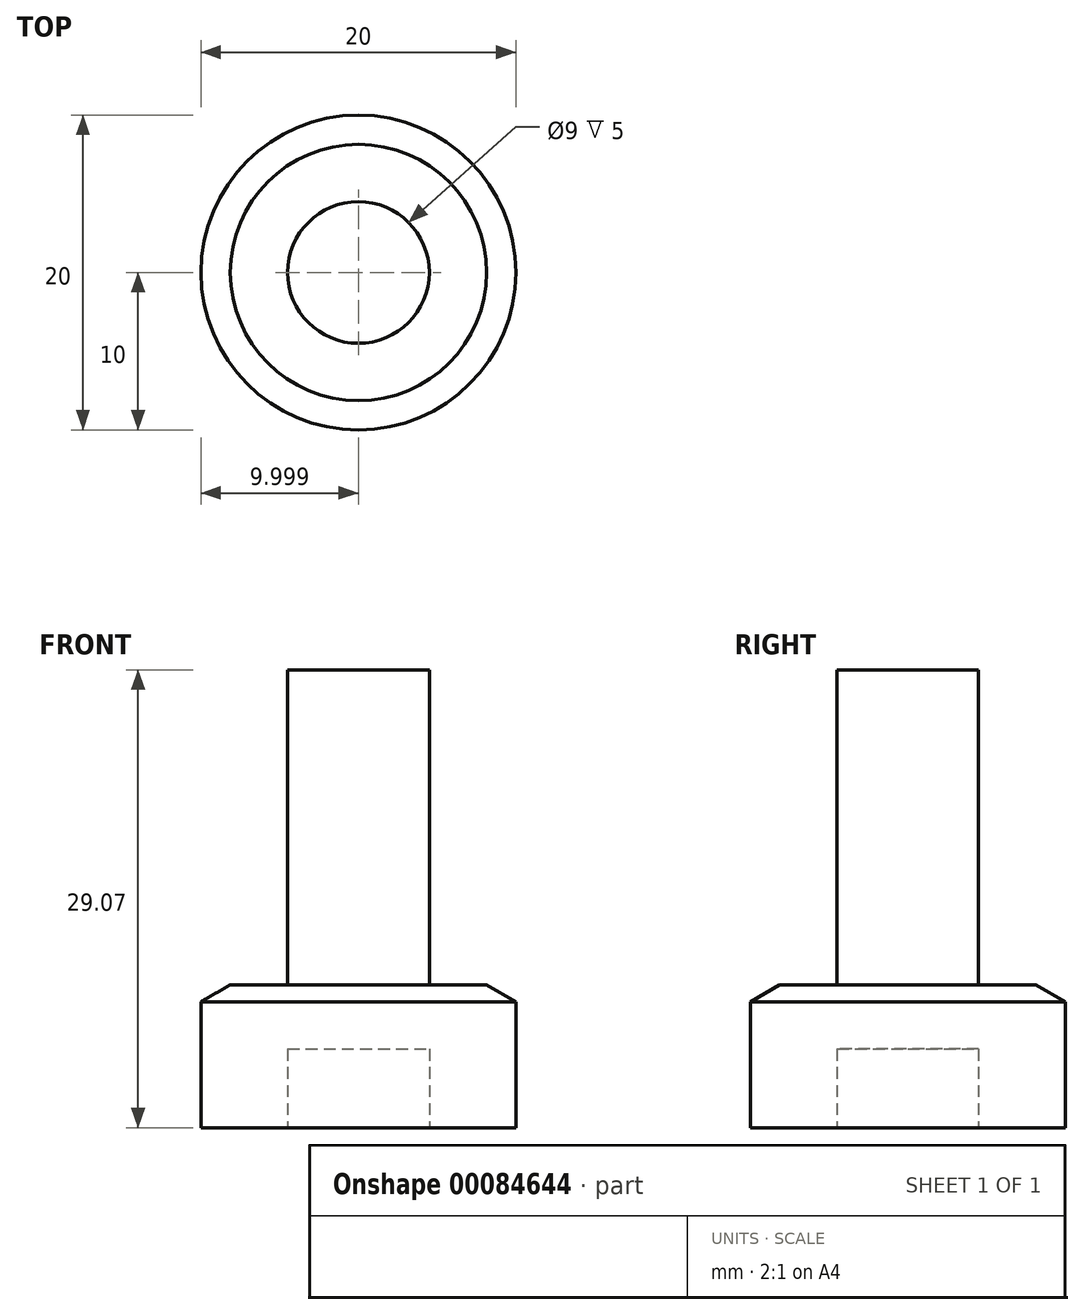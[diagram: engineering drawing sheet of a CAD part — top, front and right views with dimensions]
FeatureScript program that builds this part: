
annotation { "Feature Type Name" : "Feature", "Feature Type Description" : "" }
export const myFeature = defineFeature(function(context is Context, id is Id, definition is map)
    precondition{}
    {
        {
            var Q0;
            Q0=qCreatedBy(makeId("Front.planeOp"),FACE);
            var sketch = newSketch(context, id + "F0", { "sketchPlane" : qUnion([Q0])});
            skLineSegment(sketch, "E0.bottom", {"start": v(-30.55, 8) * mm, "end": v(-20.55, 8) * mm});
            skLineSegment(sketch, "E0.top", {"start": v(-30.55, 0) * mm, "end": v(-25.05, 0) * mm});
            skLineSegment(sketch, "E0.left", {"start": v(-30.55, 8) * mm, "end": v(-30.55, 0) * mm});
            skPoint(sketch, "E1", {"position": v(-20.55, 8) * mm});
            skPoint(sketch, "E2", {"position": v(-20.55, 0) * mm});
            skPoint(sketch, "E3", {"position": v(-20.55, 9.07) * mm});
            skLineSegment(sketch, "E4", {"start": v(-20.55, 8) * mm, "end": v(-20.55, 9.07) * mm});
            skLineSegment(sketch, "E5", {"start": v(-30.55, 8) * mm, "end": v(-28.7, 9.07) * mm});
            skLineSegment(sketch, "E6", {"start": v(-28.7, 9.07) * mm, "end": v(-20.55, 9.07) * mm});
            skLineSegment(sketch, "E7", {"start": v(-20.55, 8) * mm, "end": v(-20.55, 5) * mm});
            skPoint(sketch, "E0.right.end.orphan", {"position": v(-10.55, 0) * mm});
            skPoint(sketch, "E8.start.orphan", {"position": v(-10.55, 8) * mm});
            skLineSegment(sketch, "E9", {"start": v(-20.55, 9.07) * mm, "end": v(-20.55, 29.07) * mm});
            skLineSegment(sketch, "E10", {"start": v(-20.55, 29.07) * mm, "end": v(-25.05, 29.07) * mm});
            skLineSegment(sketch, "E11", {"start": v(-25.05, 29.07) * mm, "end": v(-25.05, 0) * mm});
            skPoint(sketch, "E12.start.orphan", {"position": v(-20.55, 4) * mm});
            skLineSegment(sketch, "E13", {"start": v(-20.55, 5) * mm, "end": v(-25.05, 5) * mm});
            skPoint(sketch, "E14", {"position": v(-20.55, 5) * mm});
            skSolve(sketch);
        }
        {
            var Q0;
            {var subQ0=sQuery(id+"F0.wireOp",EDGE,"E9");Q0=makeQuery(id+"F0.imprint","IMPRINT",FACE,{"disambiguationData":[TD([[makeQuery(id+"F0.imprint","IMPRINT",EDGE,{"derivedFrom":subQ0}),1.0]])]});}
            var Q1;
            {var subQ5=sQuery(id+"F0.wireOp",EDGE,"E0.top");Q1=makeQuery(id+"F0.imprint","IMPRINT",FACE,{"disambiguationData":[TD([[makeQuery(id+"F0.imprint","IMPRINT",EDGE,{"derivedFrom":subQ5}),1.0]])]});}
            var Q2;
            {var subQ0=sQuery(id+"F0.wireOp",EDGE,"E5");Q2=makeQuery(id+"F0.imprint","IMPRINT",FACE,{"disambiguationData":[TD([[makeQuery(id+"F0.imprint","IMPRINT",EDGE,{"derivedFrom":subQ0}),-1.0]])]});}
            var Q3;
            {var subQ0=sQuery(id+"F0.wireOp",EDGE,"E7");Q3=makeQuery(id+"F0.imprint","IMPRINT",FACE,{"disambiguationData":[TD([[makeQuery(id+"F0.imprint","IMPRINT",EDGE,{"derivedFrom":subQ0}),-1.0]])]});}
            var Q4;
            {var subQ0=sQuery(id+"F0.wireOp",EDGE,"E4");Q4=makeQuery(id+"F0.imprint","IMPRINT",FACE,{"disambiguationData":[TD([[makeQuery(id+"F0.imprint","IMPRINT",EDGE,{"derivedFrom":subQ0}),1.0]])]});}
            var Q5;
            Q5=sQuery(id+"F0.wireOp",EDGE,"E9");
            revolve(context, id + "F1", {"entities" : qUnion([Q0, Q1, Q2, Q3, Q4]), "axis" : qUnion([Q5]), "revolveType" : RevolveType.FULL});
        }
    });
